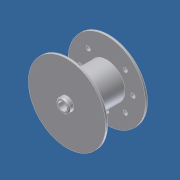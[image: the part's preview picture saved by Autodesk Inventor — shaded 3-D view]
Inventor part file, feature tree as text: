
AUTODESK INVENTOR PART (.ipt)
format: ipt  version: unknown  size: 339,968 bytes
history: native  units: in
note: dims shown in document units (in); Inventor stores cm internally (conversion verified against a paired STEP export)
features: extrude x10, sketch x10, projected_geometry x5, chamfer x2, plane x1, pattern_circular x1, reference x1
ambient origin geometry x8: Origin, YZ Plane, XZ Plane, XY Plane, X Axis, Y Axis, Z Axis, Center Point
bodies: Solid1 (feature_tree)
feature tree (30):
  extrude  "Extrusion1"  Depth=0.115in TaperAngle=0.0deg
  extrude  "Extrusion2"  Depth=2.105in TaperAngle=0.0deg
  extrude  "Extrusion3"  Depth=0.75in
  extrude  "Extrusion4"  Depth=0.49in
  sketch  "Sketch5"  dims[d12=0.75in d13=0.5in d14=0.0in]
  extrude  "Extrusion5"  Depth=0.5in TaperAngle=0.0deg
  extrude  "Extrusion6"  Depth=0.115in
  extrude  "Extrusion7"  Depth=0.0625in TaperAngle=45.0deg
  chamfer  "Chamfer1"  Distance=0.5in
  plane  "Work Plane1"
  extrude  "Extrusion8"  Depth=2.245in
  pattern_circular  "Circular Pattern1"  [2 undecoded]
  extrude  "Extrusion9"  Depth=0.025in TaperAngle=0.0deg
  chamfer  "Chamfer2"  Distance=0.025in Angle=45.0deg
  extrude  "Extrusion11"  Depth=1.0in TaperAngle=0.0deg
  sketch  "Sketch1"  dims[d0=4.315in d1=0.115in d2=0.0in]
  sketch  "Sketch2"  dims[d3=2.022in d4=2.105in d5=0.0in]
  sketch  "Sketch3"  dims[d6=0.115in d7=0.0in d8=0.75in]
  projected_geometry  "Projected Loop1"
  sketch  "Sketch4"  dims[d9=0.25in d10=0.0in d11=0.49in]
  sketch  "Sketch6"  dims[d15=0.5in d16=0.0in d17=0.115in]
  projected_geometry  "Projected Loop2"
  sketch  "Sketch7"  dims[d18=0.5in d19=0.0in d20=0.0625in d21=0.125in d22=45.0deg]
  projected_geometry  "Projected Loop3"
  sketch  "Sketch8"  dims[d23=0.575in]
  projected_geometry  "Projected Loop4"
  projected_geometry  "Projected Loop5"
  sketch  "Sketch9"  dims[d24=0.653in d25=0.5in d26=0.0in]
  sketch  "Sketch12"  dims[d27=0.7874in d28=90.0deg d30=2.245in d31=3.855in d32=0.025in d33=0.0in d34=0.025in d35=0.125in d36=45.0deg d52=1.0in d53=0.0in]
  reference  "Reference1"
note: 2 required parameter values undecoded (feature->parameter linkage not recoverable at this tier; creation-order binding heuristic only, values carry confidence <= 0.55)
